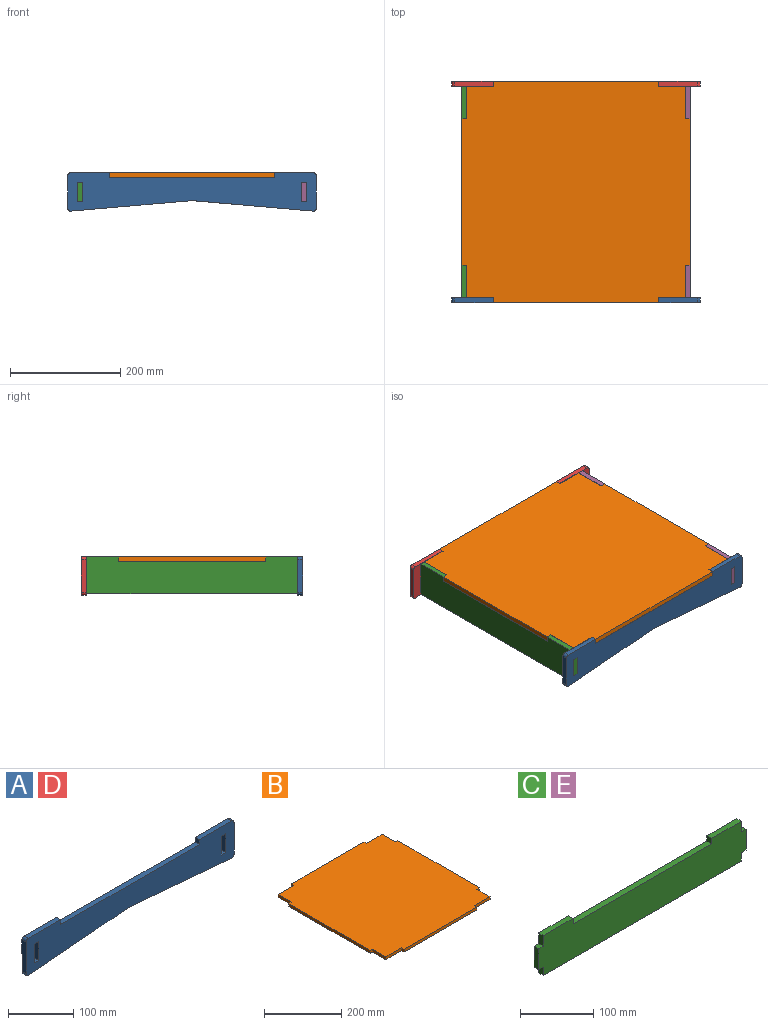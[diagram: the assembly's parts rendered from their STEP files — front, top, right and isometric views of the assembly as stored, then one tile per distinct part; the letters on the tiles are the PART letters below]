
ASSEMBLY  parts=5 mates=4
PART A: 23 faces, bbox 450x9x69.5 mm
  f0: plane 9.2x9mm, normal (0,0,-1), area 82.8mm2, adj f1,f20,f21,f22
  f1: plane 35.2x9mm, normal (-1,0,0), area 316.8mm2, adj f0,f2,f21,f22
  f2: plane 9.2x9mm, normal (0,0,1), area 82.8mm2, adj f1,f20,f21,f22
  f3: cylinder r=5mm len=9mm, axis (0,1,0), area 74.6mm2, adj f4,f18,f21,f22
  f4: plane 219.56x19.21mm, normal (0.09,0,-1), area 1983.6mm2, adj f3,f5,f21,f22
  f5: plane 219.56x19.21mm, normal (-0.09,0,-1), area 1983.6mm2, adj f4,f6,f21,f22
  f6: cylinder r=5mm len=9mm, axis (0,1,0), area 74.6mm2, adj f5,f7,f21,f22
  f7: plane 59.54x9mm, normal (1,0,0), area 535.9mm2, adj f6,f8,f21,f22
  f8: cylinder r=5mm len=9mm, axis (0,1,0), area 70.7mm2, adj f7,f9,f21,f22
  f9: plane 70x9mm, normal (0,0,1), area 630mm2, adj f8,f10,f21,f22
  f10: plane 9.2x9mm, normal (-1,0,0), area 82.8mm2, adj f9,f11,f21,f22
  f11: plane 300x9mm, normal (0,0,1), area 2700mm2, adj f10,f12,f21,f22
  f12: plane 9.2x9mm, normal (1,0,0), area 82.8mm2, adj f11,f13,f21,f22
  f13: plane 70x9mm, normal (0,0,1), area 630mm2, adj f12,f14,f21,f22
  f14: cylinder r=5mm len=9mm, axis (0,1,0), area 70.7mm2, adj f13,f18,f21,f22
  f15: plane 35.2x9mm, normal (1,0,0), area 316.8mm2, adj f16,f19,f21,f22
  f16: plane 9.2x9mm, normal (0,0,-1), area 82.8mm2, adj f15,f17,f21,f22
  f17: plane 35.2x9mm, normal (-1,0,0), area 316.8mm2, adj f16,f19,f21,f22
  f18: plane 59.54x9mm, normal (-1,0,0), area 535.9mm2, adj f3,f14,f21,f22
  f19: plane 9.2x9mm, normal (0,0,1), area 82.8mm2, adj f15,f17,f21,f22
  f20: plane 35.2x9mm, normal (1,0,0), area 316.8mm2, adj f0,f2,f21,f22
  f21: plane 450x69.54mm, normal (0,-1,0), area 23639.4mm2, adj f0,f1,f2,f3,f4,f5,f6,f7
  f22: plane 450x69.54mm, normal (0,1,0), area 23639.4mm2, adj f0,f1,f2,f3,f4,f5,f6,f7
PART B: 22 faces, bbox 400x413.6x9 mm
  f0: plane 9x9mm, normal (0,-1,0), area 81mm2, adj f1,f19,f20,f21
  f1: plane 48x9mm, normal (-1,0,0), area 432mm2, adj f0,f2,f20,f21
  f2: plane 57.87x9mm, normal (0,-1,0), area 520.8mm2, adj f1,f3,f20,f21
  f3: plane 9x9mm, normal (-1,0,0), area 81mm2, adj f2,f4,f20,f21
  f4: plane 266.27x9mm, normal (0,-1,0), area 2396.4mm2, adj f3,f5,f20,f21
  f5: plane 9x9mm, normal (1,0,0), area 81mm2, adj f4,f6,f20,f21
  f6: plane 57.87x9mm, normal (0,-1,0), area 520.8mm2, adj f5,f7,f20,f21
  f7: plane 48x9mm, normal (1,0,0), area 432mm2, adj f6,f8,f20,f21
  f8: plane 9x9mm, normal (0,-1,0), area 81mm2, adj f7,f9,f20,f21
  f9: plane 299.6x9mm, normal (1,0,0), area 2696.4mm2, adj f8,f10,f20,f21
  f10: plane 9x9mm, normal (0,1,0), area 81mm2, adj f9,f11,f20,f21
  f11: plane 48x9mm, normal (1,0,0), area 432mm2, adj f10,f12,f20,f21
  f12: plane 57.87x9mm, normal (0,1,0), area 520.8mm2, adj f11,f13,f20,f21
  f13: plane 9x9mm, normal (1,0,0), area 81mm2, adj f12,f14,f20,f21
  f14: plane 266.27x9mm, normal (0,1,0), area 2396.4mm2, adj f13,f15,f20,f21
  f15: plane 9x9mm, normal (-1,0,0), area 81mm2, adj f14,f16,f20,f21
  f16: plane 57.87x9mm, normal (0,1,0), area 520.8mm2, adj f15,f17,f20,f21
  f17: plane 48x9mm, normal (-1,0,0), area 432mm2, adj f16,f18,f20,f21
  f18: plane 9x9mm, normal (0,1,0), area 81mm2, adj f17,f19,f20,f21
  f19: plane 299.6x9mm, normal (-1,0,0), area 2696.4mm2, adj f0,f18,f20,f21
  f20: plane 413.6x400mm, normal (0,0,1), area 161304.8mm2, adj f0,f1,f2,f3,f4,f5,f6,f7
  f21: plane 413.6x400mm, normal (0,0,-1), area 161304.8mm2, adj f0,f1,f2,f3,f4,f5,f6,f7
PART C: 18 faces, bbox 400x9x66.5 mm
  f0: plane 17.5x9mm, normal (1,0,0), area 157.5mm2, adj f1,f15,f16,f17
  f1: plane 57.47x9mm, normal (0,0,1), area 517.2mm2, adj f0,f2,f16,f17
  f2: plane 9x9mm, normal (-1,0,0), area 81mm2, adj f1,f3,f16,f17
  f3: plane 267.07x9mm, normal (0,0,1), area 2403.6mm2, adj f2,f4,f16,f17
  f4: plane 9x9mm, normal (1,0,0), area 81mm2, adj f3,f5,f16,f17
  f5: plane 57.47x9mm, normal (0,0,1), area 517.2mm2, adj f4,f6,f16,f17
  f6: plane 17.5x9mm, normal (-1,0,0), area 157.5mm2, adj f5,f7,f16,f17
  f7: plane 9x9mm, normal (0,0,1), area 81mm2, adj f6,f8,f16,f17
  f8: plane 35x9mm, normal (-1,0,0), area 315mm2, adj f7,f9,f16,f17
  f9: plane 9x9mm, normal (0,0,-1), area 81mm2, adj f8,f10,f16,f17
  f10: plane 14x9mm, normal (-1,0,0), area 126mm2, adj f9,f11,f16,f17
  f11: plane 382x9mm, normal (0,0,-1), area 3438mm2, adj f10,f12,f16,f17
  f12: plane 14x9mm, normal (1,0,0), area 126mm2, adj f11,f13,f16,f17
  f13: plane 9x9mm, normal (0,0,-1), area 81mm2, adj f12,f14,f16,f17
  f14: plane 35x9mm, normal (1,0,0), area 315mm2, adj f13,f15,f16,f17
  f15: plane 9x9mm, normal (0,0,1), area 81mm2, adj f0,f14,f16,f17
  f16: plane 400x66.5mm, normal (0,-1,0), area 23629.4mm2, adj f0,f1,f2,f3,f4,f5,f6,f7
  f17: plane 400x66.5mm, normal (0,1,0), area 23629.4mm2, adj f0,f1,f2,f3,f4,f5,f6,f7
PART D: same geometry as A
PART E: same geometry as C
PLACE A rot(axis=(-0.01,0.24,0.97),0deg) t=(-275.92,95.8,-68.27)mm
PLACE B rot(axis=(0,0,1),90deg) t=(-51.02,287.2,-7.47)mm
PLACE C rot(axis=(0,0,1),90deg) t=(-257.82,286.8,-114.9)mm
PLACE D rot(axis=(-0.12,0.75,-0.65),0deg) t=(-276.12,487.6,-68.27)mm
PLACE E rot(axis=(0,0,1),90deg) t=(146.78,287.6,-114.9)mm
MATE fastened C.f2 <-> B.f13  axis (0,-1,0) through (-253.32,420.33,-2.97)mm
MATE fastened D.f2 <-> E.f13  axis (0,0,1) through (151.28,483.1,-50.97)mm
MATE fastened C.f9 <-> A.f19  axis (0,0,-1) through (-253.32,91.3,-50.97)mm
MATE fastened E.f4 <-> B.f3  axis (0,1,0) through (151.28,154.07,-2.97)mm
